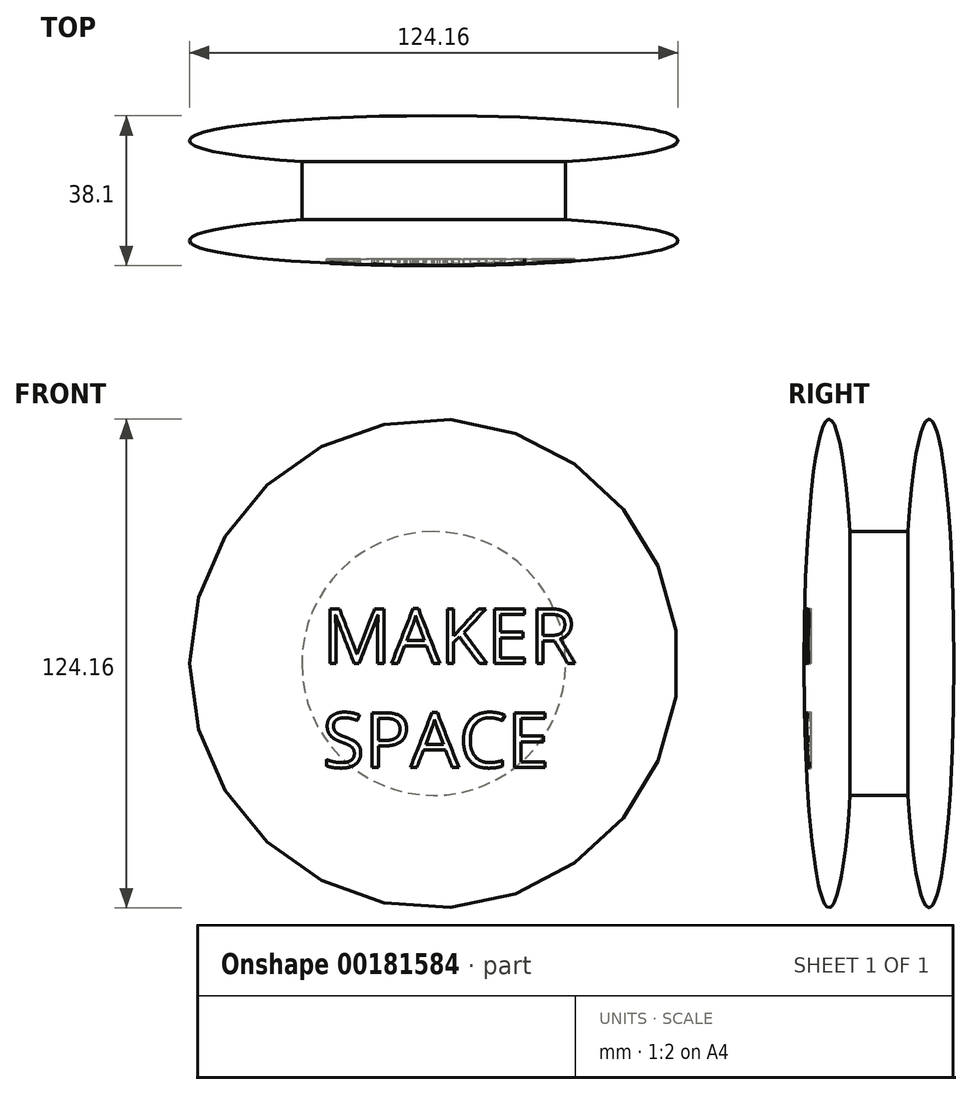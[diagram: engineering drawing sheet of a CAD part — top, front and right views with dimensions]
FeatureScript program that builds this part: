
annotation { "Feature Type Name" : "Feature", "Feature Type Description" : "" }
export const myFeature = defineFeature(function(context is Context, id is Id, definition is map)
    precondition{}
    {
        {
            var Q0;
            Q0=qCreatedBy(makeId("Top.planeOp"),FACE);
            var sketch = newSketch(context, id + "F0", { "sketchPlane" : qUnion([Q0])});
            skEllipticalArc(sketch, "E0", {});
            skEllipticalArc(sketch, "E1", {});
            skLineSegment(sketch, "E2", {"start": v(0, -20.77) * mm, "end": v(0, -46.17) * mm});
            skLineSegment(sketch, "E3", {"start": v(-62.08, -20.77) * mm, "end": v(0, -20.77) * mm});
            skLineSegment(sketch, "E4", {"start": v(-62.08, -46.17) * mm, "end": v(0, -46.17) * mm});
            skLineSegment(sketch, "E5", {"start": v(-33.52, -20.77) * mm, "end": v(-33.52, -46.17) * mm});
            skLineSegment(sketch, "E6", {"start": v(0, -14.42) * mm, "end": v(0, -52.52) * mm});
            skPoint(sketch, "E7.orphan", {"position": v(62.08, -20.77) * mm});
            skPoint(sketch, "E8.orphan", {"position": v(62.08, -46.17) * mm});
            const initialGuessF0  = {"E0": [0, -0.0207733303964138, -1, 0, 0.062076901191756156, 0.00635, 4.71238898038469, 1.5707963267948966], "E1": [0, -0.0461733303964138, -1, 0, 0.062076901191756156, 0.00635, 4.71238898038469, 1.5707963267948966]};
            skSetInitialGuess(sketch, initialGuessF0);
            skSolve(sketch);
        }
        {
            var Q0;
            Q0 = qSketchRegion(id + "F0", true);
            var Q1;
            Q1=sQuery(id+"F0.wireOp",EDGE,"E6");
            revolve(context, id + "F1", {"entities" : qUnion([Q0]), "axis" : qUnion([Q1]), "revolveType" : RevolveType.FULL});
        }
        {
            var Q0;
            Q0=qCreatedBy(makeId("Front.planeOp"),FACE);
            cPlane(context, id + "F2", {"entities" : qUnion([Q0]), "cplaneType" : CPlaneType.OFFSET, "offset" : 50.8 * mm, "width" : 152.4 * mm, "height" : 152.4 * mm});
        }
        {
            var Q0;
            Q0=qCreatedBy(id+"F2.planeOp",FACE);
            var sketch = newSketch(context, id + "F3", { "sketchPlane" : qUnion([Q0])});
            skText(sketch, "E9", { "text": "MAKER \nSPACE\n", "fontName": "OpenSans-Regular.ttf"});
            const initialGuessF3  = {"E9": [-0.02827, 0, 1, 0, 0.01398]};
            skSetInitialGuess(sketch, initialGuessF3);
            skSolve(sketch);
        }
        {
            var Q0;
            Q0 = qSketchRegion(id + "F3", true);
            extrude(context, id + "F4", {"entities" : qUnion([Q0]), "operationType" : NewBodyOperationType.REMOVE, "depth" : 25.4 * mm});
        }
    });
